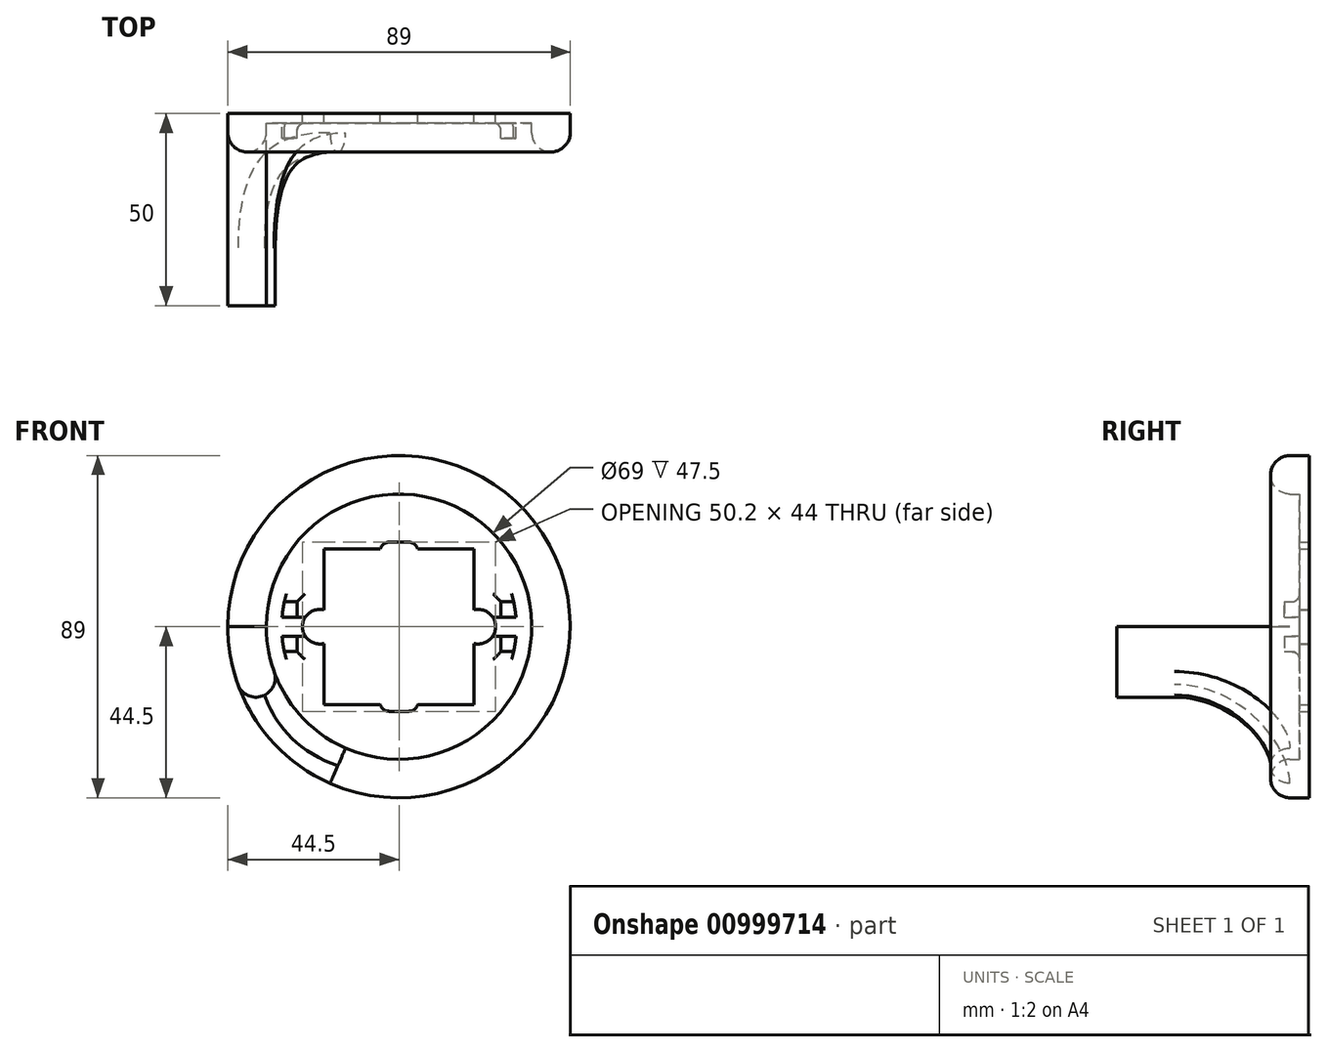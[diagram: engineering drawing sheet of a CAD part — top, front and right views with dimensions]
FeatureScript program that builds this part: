
annotation { "Feature Type Name" : "Feature", "Feature Type Description" : "" }
export const myFeature = defineFeature(function(context is Context, id is Id, definition is map)
    precondition{}
    {
        {
            var Q0;
            Q0=qCreatedBy(makeId("Front.planeOp"),FACE);
            var sketch = newSketch(context, id + "F0", { "sketchPlane" : qUnion([Q0])});
            skCircle(sketch, "E0", {"center": v(0, 0) * mm, "radius": 34.5 * mm});
            skCircle(sketch, "E1", {"center": v(0, 0) * mm, "radius": 44.5 * mm});
            skLineSegment(sketch, "E2", {"start": v(30.74, -15.66) * mm, "end": v(39.65, -20.2) * mm});
            skLineSegment(sketch, "E3", {"start": v(34.5, 0) * mm, "end": v(44.5, 0) * mm});
            skCircle(sketch, "E4", {"center": v(-20.6, 0) * mm, "radius": 4.5 * mm});
            skCircle(sketch, "E5.MirrorC", {"center": v(20.6, 0) * mm, "radius": 4.5 * mm});
            skCircle(sketch, "E6", {"center": v(0, 0) * mm, "radius": 16 * mm});
            skArc(sketch, "E7", {"start": v(2.5, 17) * mm, "mid": v(5, 19.5) * mm, "end": v(2.5, 22) * mm});
            skLineSegment(sketch, "E8", {"start": v(2.5, 22) * mm, "end": v(0, 22) * mm});
            skLineSegment(sketch, "E9", {"start": v(2.5, 17) * mm, "end": v(0, 17) * mm});
            skLineSegment(sketch, "E10.MirrorCS", {"start": v(-2.5, 17) * mm, "end": v(0, 17) * mm});
            skArc(sketch, "E11.MirrorCS", {"start": v(-2.5, 17) * mm, "mid": v(-5, 19.5) * mm, "end": v(-2.5, 22) * mm});
            skLineSegment(sketch, "E12.MirrorCS", {"start": v(-2.5, 22) * mm, "end": v(0, 22) * mm});
            skLineSegment(sketch, "E13.MirrorCS", {"start": v(-2.5, -17) * mm, "end": v(0, -17) * mm});
            skArc(sketch, "E14.MirrorCS", {"start": v(2.5, -17) * mm, "mid": v(5, -19.5) * mm, "end": v(2.5, -22) * mm});
            skArc(sketch, "E15.MirrorCS", {"start": v(-2.5, -17) * mm, "mid": v(-5, -19.5) * mm, "end": v(-2.5, -22) * mm});
            skLineSegment(sketch, "E16.MirrorCS", {"start": v(2.5, -17) * mm, "end": v(0, -17) * mm});
            skLineSegment(sketch, "E17.MirrorCS", {"start": v(-2.5, -22) * mm, "end": v(0, -22) * mm});
            skLineSegment(sketch, "E18.MirrorCS", {"start": v(2.5, -22) * mm, "end": v(0, -22) * mm});
            skLineSegment(sketch, "E19.trimOffspring", {"start": v(19.5, 20.25) * mm, "end": v(-19.5, 20.25) * mm});
            skLineSegment(sketch, "E20.trimOffspring", {"start": v(-19.5, 20.25) * mm, "end": v(-19.5, -20.25) * mm});
            skLineSegment(sketch, "E21.trimOffspring", {"start": v(19.5, 20.25) * mm, "end": v(19.5, -20.25) * mm});
            skLineSegment(sketch, "E22.trimOffspring", {"start": v(19.5, -20.25) * mm, "end": v(-19.5, -20.25) * mm});
            skPoint(sketch, "E23.trimOffspring.end.orphan", {"position": v(19.5, -59.57) * mm});
            skPoint(sketch, "E24.trimOffspring.end.orphan", {"position": v(-19.5, -59.57) * mm});
            skPoint(sketch, "E25.start.orphan", {"position": v(-19.5, 57.03) * mm});
            skPoint(sketch, "E26.MirrorCS.start.orphan", {"position": v(19.5, 57.03) * mm});
            skLineSegment(sketch, "E27", {"start": v(-30.4, 2.5) * mm, "end": v(-26.5, 2.5) * mm});
            skLineSegment(sketch, "E28", {"start": v(-26.5, 2.5) * mm, "end": v(-26.5, 6.5) * mm});
            skLineSegment(sketch, "E29", {"start": v(-26.5, 6.5) * mm, "end": v(-29.8, 6.5) * mm});
            skLineSegment(sketch, "E30.MirrorCS", {"start": v(-30.4, -2.5) * mm, "end": v(-26.5, -2.5) * mm});
            skLineSegment(sketch, "E31.MirrorCS", {"start": v(-26.5, -2.5) * mm, "end": v(-26.5, -6.5) * mm});
            skLineSegment(sketch, "E32.MirrorCS", {"start": v(-26.5, -6.5) * mm, "end": v(-29.8, -6.5) * mm});
            skLineSegment(sketch, "E33.MirrorCS", {"start": v(26.5, -6.5) * mm, "end": v(29.8, -6.5) * mm});
            skLineSegment(sketch, "E34.MirrorCS", {"start": v(26.5, -2.5) * mm, "end": v(26.5, -6.5) * mm});
            skLineSegment(sketch, "E35.MirrorCS", {"start": v(30.4, -2.5) * mm, "end": v(26.5, -2.5) * mm});
            skLineSegment(sketch, "E36.MirrorCS", {"start": v(30.4, 2.5) * mm, "end": v(26.5, 2.5) * mm});
            skLineSegment(sketch, "E37.MirrorCS", {"start": v(26.5, 2.5) * mm, "end": v(26.5, 6.5) * mm});
            skLineSegment(sketch, "E38.MirrorCS", {"start": v(26.5, 6.5) * mm, "end": v(29.8, 6.5) * mm});
            skCircle(sketch, "E39", {"center": v(0, 0) * mm, "radius": 30.5 * mm});
            skPoint(sketch, "E40.orphan", {"position": v(-34.4, 2.5) * mm});
            skPoint(sketch, "E41.orphan", {"position": v(-33.88, 6.5) * mm});
            skPoint(sketch, "E42.orphan", {"position": v(-34.4, -2.5) * mm});
            skPoint(sketch, "E43.orphan", {"position": v(-33.88, -6.5) * mm});
            skPoint(sketch, "E44.orphan", {"position": v(34.4, 2.5) * mm});
            skPoint(sketch, "E45.orphan", {"position": v(33.88, 6.5) * mm});
            skPoint(sketch, "E46.orphan", {"position": v(33.88, -6.5) * mm});
            skPoint(sketch, "E47.orphan", {"position": v(34.4, -2.5) * mm});
            skLineSegment(sketch, "E48.MirrorCS", {"start": v(-34.5, 0) * mm, "end": v(-44.5, 0) * mm});
            skLineSegment(sketch, "E49.MirrorCS", {"start": v(-30.74, -15.66) * mm, "end": v(-39.65, -20.2) * mm});
            skSolve(sketch);
        }
        {
            var Q0;
            Q0=makeQuery(id+"F0.imprint","IMPRINT",FACE,{"disambiguationData":[TD([[makeQuery(id+"F0.imprint","IMPRINT",EDGE,{"derivedFrom":sQuery(id+"F0.wireOp",EDGE,"E0")}),-1.0]])]});
            extrude(context, id + "F1", {"entities" : qUnion([Q0]), "depth" : 10 * mm, "offsetDistance" : 25 * mm});
        }
        {
            var Q0;
            {var subQ0=sQuery(id+"F0.wireOp",EDGE,"E48.MirrorCS");Q0=makeQuery(id+"F0.imprint","IMPRINT",FACE,{"disambiguationData":[TD([[makeQuery(id+"F0.imprint","IMPRINT",EDGE,{"derivedFrom":subQ0}),1.0]])]});}
            extrude(context, id + "F2", {"entities" : qUnion([Q0]), "operationType" : NewBodyOperationType.ADD, "depth" : 50 * mm, "offsetDistance" : 25 * mm});
        }
        {
            var Q0;
            {var subQ0=sQuery(id+"F0.wireOp",EDGE,"E0");var subQ1=makeQuery(id+"F0.imprint","INTERSECT",VERTEX,{"derivedFrom":[subQ0,sQuery(id+"F0.wireOp",EDGE,"E2")]});Q0=makeQuery(id+"F0.imprint","IMPRINT",FACE,{"disambiguationData":[TD([[makeQuery(id+"F0.imprint","IMPRINT",EDGE,{"disambiguationData":[TD([[subQ1,1.0]])],"derivedFrom":subQ0}),1.0]])]});}
            var Q1;
            {var subQ0=sQuery(id+"F0.wireOp",EDGE,"E27");Q1=makeQuery(id+"F0.imprint","IMPRINT",FACE,{"disambiguationData":[TD([[makeQuery(id+"F0.imprint","IMPRINT",EDGE,{"derivedFrom":subQ0}),1.0]])]});}
            var Q2;
            {var subQ0=sQuery(id+"F0.wireOp",EDGE,"E30.MirrorCS");Q2=makeQuery(id+"F0.imprint","IMPRINT",FACE,{"disambiguationData":[TD([[makeQuery(id+"F0.imprint","IMPRINT",EDGE,{"derivedFrom":subQ0}),-1.0]])]});}
            var Q3;
            {var subQ0=sQuery(id+"F0.wireOp",EDGE,"E36.MirrorCS");Q3=makeQuery(id+"F0.imprint","IMPRINT",FACE,{"disambiguationData":[TD([[makeQuery(id+"F0.imprint","IMPRINT",EDGE,{"derivedFrom":subQ0}),-1.0]])]});}
            var Q4;
            {var subQ0=sQuery(id+"F0.wireOp",EDGE,"E33.MirrorCS");Q4=makeQuery(id+"F0.imprint","IMPRINT",FACE,{"disambiguationData":[TD([[makeQuery(id+"F0.imprint","IMPRINT",EDGE,{"derivedFrom":subQ0}),1.0]])]});}
            var Q5;
            {var subQ15=sQuery(id+"F0.wireOp",EDGE,"E27");Q5=makeQuery(id+"F0.imprint","IMPRINT",FACE,{"disambiguationData":[TD([[makeQuery(id+"F0.imprint","IMPRINT",EDGE,{"derivedFrom":subQ15}),-1.0]])]});}
            extrude(context, id + "F3", {"entities" : qUnion([Q0, Q1, Q2, Q3, Q4, Q5]), "operationType" : NewBodyOperationType.ADD, "depth" : 2.5 * mm, "offsetDistance" : 25 * mm});
        }
        {
            var Q0;
            {var subQ0=sQuery(id+"F0.wireOp",EDGE,"E27");Q0=makeQuery(id+"F0.imprint","IMPRINT",FACE,{"disambiguationData":[TD([[makeQuery(id+"F0.imprint","IMPRINT",EDGE,{"derivedFrom":subQ0}),1.0]])]});}
            var Q1;
            {var subQ0=sQuery(id+"F0.wireOp",EDGE,"E30.MirrorCS");Q1=makeQuery(id+"F0.imprint","IMPRINT",FACE,{"disambiguationData":[TD([[makeQuery(id+"F0.imprint","IMPRINT",EDGE,{"derivedFrom":subQ0}),-1.0]])]});}
            var Q2;
            {var subQ0=sQuery(id+"F0.wireOp",EDGE,"E36.MirrorCS");Q2=makeQuery(id+"F0.imprint","IMPRINT",FACE,{"disambiguationData":[TD([[makeQuery(id+"F0.imprint","IMPRINT",EDGE,{"derivedFrom":subQ0}),-1.0]])]});}
            var Q3;
            {var subQ0=sQuery(id+"F0.wireOp",EDGE,"E33.MirrorCS");Q3=makeQuery(id+"F0.imprint","IMPRINT",FACE,{"disambiguationData":[TD([[makeQuery(id+"F0.imprint","IMPRINT",EDGE,{"derivedFrom":subQ0}),1.0]])]});}
            extrude(context, id + "F4", {"entities" : qUnion([Q0, Q1, Q2, Q3]), "operationType" : NewBodyOperationType.ADD, "depth" : 6.5 * mm, "offsetDistance" : 25 * mm});
        }
        {
            var Q0;
            Q0=makeQuery(id+"F4.boolean.opBoolean","INTERSECT",EDGE,{"derivedFrom":[makeQuery(id+"F3.opExtrude","CAP_FACE",FACE,{"disambiguationData":[OSD([sQuery(id+"F0.wireOp",EDGE,"E0"),sQuery(id+"F0.wireOp",EDGE,"E4"),sQuery(id+"F0.wireOp",EDGE,"E5.MirrorC"),sQuery(id+"F0.wireOp",EDGE,"E19.trimOffspring"),sQuery(id+"F0.wireOp",EDGE,"E20.trimOffspring"),sQuery(id+"F0.wireOp",EDGE,"E21.trimOffspring"),sQuery(id+"F0.wireOp",EDGE,"E22.trimOffspring")])],"isStart":false}),makeQuery(id+"F4.opExtrude","SWEPT_FACE",FACE,{"disambiguationData":[OSD([sQuery(id+"F0.wireOp",EDGE,"E28")])]})]});
            var Q1;
            Q1=makeQuery(id+"F4.boolean.opBoolean","INTERSECT",EDGE,{"derivedFrom":[makeQuery(id+"F3.opExtrude","CAP_FACE",FACE,{"disambiguationData":[OSD([sQuery(id+"F0.wireOp",EDGE,"E0"),sQuery(id+"F0.wireOp",EDGE,"E4"),sQuery(id+"F0.wireOp",EDGE,"E5.MirrorC"),sQuery(id+"F0.wireOp",EDGE,"E19.trimOffspring"),sQuery(id+"F0.wireOp",EDGE,"E20.trimOffspring"),sQuery(id+"F0.wireOp",EDGE,"E21.trimOffspring"),sQuery(id+"F0.wireOp",EDGE,"E22.trimOffspring")])],"isStart":false}),makeQuery(id+"F4.opExtrude","SWEPT_FACE",FACE,{"disambiguationData":[OSD([sQuery(id+"F0.wireOp",EDGE,"E29")])]})]});
            var Q2;
            Q2=makeQuery(id+"F4.boolean.opBoolean","INTERSECT",EDGE,{"derivedFrom":[makeQuery(id+"F3.opExtrude","CAP_FACE",FACE,{"disambiguationData":[OSD([sQuery(id+"F0.wireOp",EDGE,"E0"),sQuery(id+"F0.wireOp",EDGE,"E4"),sQuery(id+"F0.wireOp",EDGE,"E5.MirrorC"),sQuery(id+"F0.wireOp",EDGE,"E19.trimOffspring"),sQuery(id+"F0.wireOp",EDGE,"E20.trimOffspring"),sQuery(id+"F0.wireOp",EDGE,"E21.trimOffspring"),sQuery(id+"F0.wireOp",EDGE,"E22.trimOffspring")])],"isStart":false}),makeQuery(id+"F4.opExtrude","SWEPT_FACE",FACE,{"disambiguationData":[OSD([sQuery(id+"F0.wireOp",EDGE,"E31.MirrorCS")])]})]});
            var Q3;
            Q3=makeQuery(id+"F4.boolean.opBoolean","INTERSECT",EDGE,{"derivedFrom":[makeQuery(id+"F3.opExtrude","CAP_FACE",FACE,{"disambiguationData":[OSD([sQuery(id+"F0.wireOp",EDGE,"E0"),sQuery(id+"F0.wireOp",EDGE,"E4"),sQuery(id+"F0.wireOp",EDGE,"E5.MirrorC"),sQuery(id+"F0.wireOp",EDGE,"E19.trimOffspring"),sQuery(id+"F0.wireOp",EDGE,"E20.trimOffspring"),sQuery(id+"F0.wireOp",EDGE,"E21.trimOffspring"),sQuery(id+"F0.wireOp",EDGE,"E22.trimOffspring")])],"isStart":false}),makeQuery(id+"F4.opExtrude","SWEPT_FACE",FACE,{"disambiguationData":[OSD([sQuery(id+"F0.wireOp",EDGE,"E32.MirrorCS")])]})]});
            var Q4;
            Q4=makeQuery(id+"F4.boolean.opBoolean","INTERSECT",EDGE,{"derivedFrom":[makeQuery(id+"F3.opExtrude","CAP_FACE",FACE,{"disambiguationData":[OSD([sQuery(id+"F0.wireOp",EDGE,"E0"),sQuery(id+"F0.wireOp",EDGE,"E4"),sQuery(id+"F0.wireOp",EDGE,"E5.MirrorC"),sQuery(id+"F0.wireOp",EDGE,"E19.trimOffspring"),sQuery(id+"F0.wireOp",EDGE,"E20.trimOffspring"),sQuery(id+"F0.wireOp",EDGE,"E21.trimOffspring"),sQuery(id+"F0.wireOp",EDGE,"E22.trimOffspring")])],"isStart":false}),makeQuery(id+"F4.opExtrude","SWEPT_FACE",FACE,{"disambiguationData":[OSD([sQuery(id+"F0.wireOp",EDGE,"E33.MirrorCS")])]})]});
            var Q5;
            Q5=makeQuery(id+"F4.boolean.opBoolean","INTERSECT",EDGE,{"derivedFrom":[makeQuery(id+"F3.opExtrude","CAP_FACE",FACE,{"disambiguationData":[OSD([sQuery(id+"F0.wireOp",EDGE,"E0"),sQuery(id+"F0.wireOp",EDGE,"E4"),sQuery(id+"F0.wireOp",EDGE,"E5.MirrorC"),sQuery(id+"F0.wireOp",EDGE,"E19.trimOffspring"),sQuery(id+"F0.wireOp",EDGE,"E20.trimOffspring"),sQuery(id+"F0.wireOp",EDGE,"E21.trimOffspring"),sQuery(id+"F0.wireOp",EDGE,"E22.trimOffspring")])],"isStart":false}),makeQuery(id+"F4.opExtrude","SWEPT_FACE",FACE,{"disambiguationData":[OSD([sQuery(id+"F0.wireOp",EDGE,"E34.MirrorCS")])]})]});
            var Q6;
            Q6=makeQuery(id+"F4.boolean.opBoolean","INTERSECT",EDGE,{"derivedFrom":[makeQuery(id+"F3.opExtrude","CAP_FACE",FACE,{"disambiguationData":[OSD([sQuery(id+"F0.wireOp",EDGE,"E0"),sQuery(id+"F0.wireOp",EDGE,"E4"),sQuery(id+"F0.wireOp",EDGE,"E5.MirrorC"),sQuery(id+"F0.wireOp",EDGE,"E19.trimOffspring"),sQuery(id+"F0.wireOp",EDGE,"E20.trimOffspring"),sQuery(id+"F0.wireOp",EDGE,"E21.trimOffspring"),sQuery(id+"F0.wireOp",EDGE,"E22.trimOffspring")])],"isStart":false}),makeQuery(id+"F4.opExtrude","SWEPT_FACE",FACE,{"disambiguationData":[OSD([sQuery(id+"F0.wireOp",EDGE,"E37.MirrorCS")])]})]});
            var Q7;
            Q7=makeQuery(id+"F4.boolean.opBoolean","INTERSECT",EDGE,{"derivedFrom":[makeQuery(id+"F3.opExtrude","CAP_FACE",FACE,{"disambiguationData":[OSD([sQuery(id+"F0.wireOp",EDGE,"E0"),sQuery(id+"F0.wireOp",EDGE,"E4"),sQuery(id+"F0.wireOp",EDGE,"E5.MirrorC"),sQuery(id+"F0.wireOp",EDGE,"E19.trimOffspring"),sQuery(id+"F0.wireOp",EDGE,"E20.trimOffspring"),sQuery(id+"F0.wireOp",EDGE,"E21.trimOffspring"),sQuery(id+"F0.wireOp",EDGE,"E22.trimOffspring")])],"isStart":false}),makeQuery(id+"F4.opExtrude","SWEPT_FACE",FACE,{"disambiguationData":[OSD([sQuery(id+"F0.wireOp",EDGE,"E38.MirrorCS")])]})]});
            fillet(context, id + "F5", {"entities" : qUnion([Q0, Q1, Q2, Q3, Q4, Q5, Q6, Q7]), "radius" : 2 * mm, "tangentPropagation" : true, "allowEdgeOverflow" : false});
        }
        {
            var Q0;
            Q0=makeQuery(id+"F2.boolean.opBoolean","INTERSECT",EDGE,{"derivedFrom":[makeQuery(id+"F1.opExtrude","CAP_FACE",FACE,{"disambiguationData":[OSD([sQuery(id+"F0.wireOp",EDGE,"E0"),sQuery(id+"F0.wireOp",EDGE,"E1")])],"isStart":false}),makeQuery(id+"F2.opExtrude","SWEPT_FACE",FACE,{"disambiguationData":[OSD([sQuery(id+"F0.wireOp",EDGE,"E49.MirrorCS")])]})]});
            fillet(context, id + "F6", {"entities" : qUnion([Q0]), "radius" : 25 * mm, "tangentPropagation" : true, "allowEdgeOverflow" : false});
        }
        {
            var Q0;
            Q0=makeQuery(id+"F1.opExtrude","CAP_EDGE",EDGE,{"disambiguationData":[OSD([sQuery(id+"F0.wireOp",EDGE,"E1")])],"isStart":false});
            var Q1;
            Q1=makeQuery(id+"F1.opExtrude","CAP_EDGE",EDGE,{"disambiguationData":[OSD([sQuery(id+"F0.wireOp",EDGE,"E0")])],"isStart":false});
            fillet(context, id + "F7", {"entities" : qUnion([Q0, Q1]), "radius" : 5 * mm, "tangentPropagation" : true, "allowEdgeOverflow" : false});
        }
    });
